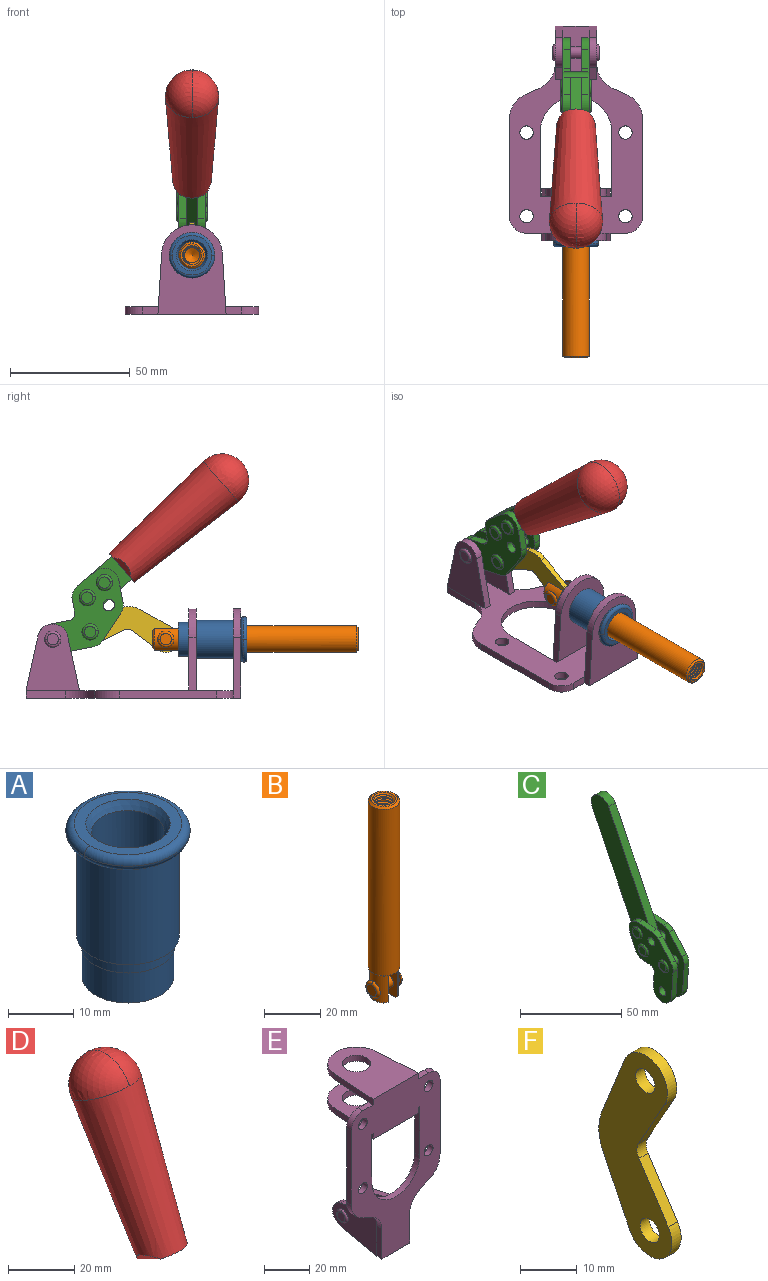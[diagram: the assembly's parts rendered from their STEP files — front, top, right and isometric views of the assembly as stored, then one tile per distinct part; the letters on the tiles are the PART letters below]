
ASSEMBLY  parts=6 mates=6
PART A: 15 faces, bbox 20.6x20.6x28.7 mm
  f0: torus R=8.26mm, axis (0,0,1), area 56.8mm2, adj f1,f10,f12
  f1: torus R=8.26mm, axis (0,0,1), area 56.8mm2, adj f0,f6,f13
  f2: cylinder r=5.59mm len=25.91mm, axis (0,0,1), area 909.6mm2, adj f3,f4
  f3: cone r=6.86mm half-angle=45deg, axis (0,0,-1), area 70.2mm2, adj f2,f14
  f4: cone r=6.47mm half-angle=30deg, axis (0,0,1), area 66.7mm2, adj f2,f13
  f5: cylinder r=7.04mm len=14.07mm, axis (0,0,1), area 252.6mm2, adj f11,f14
  f6: torus R=8.26mm, axis (0,0,1), area 56.8mm2, adj f1,f12,f13
  f7: cylinder r=7.16mm len=14.33mm, axis (0,0,1), area 91.5mm2, adj f9,f11
  f8: cylinder r=7.86mm len=18.42mm, axis (0,0,1), area 909.6mm2, adj f9,f10
  f9: plane 15.72x15.72mm, normal (0,0,-1), area 33mm2, adj f7,f8
  f10: plane 16.51x16.51mm, normal (0,0,-1), area 19.9mm2, adj f0,f8,f12
  f11: plane 14.33x14.33mm, normal (0,0,-1), area 5.7mm2, adj f5,f7
  f12: torus R=8.26mm, axis (0,0,1), area 56.8mm2, adj f0,f6,f10
  f13: plane 16.51x16.51mm, normal (0,0,1), area 82.7mm2, adj f1,f4,f6
  f14: plane 14.07x14.07mm, normal (0,0,-1), area 7.8mm2, adj f3,f5
PART B: 48 faces, bbox 12.6x11.1x86.1 mm
  f0: torus R=2.41mm, axis (-1,0,0), area 15mm2, adj f30,f32,f34
  f1: torus R=2.41mm, axis (-1,0,0), area 15mm2, adj f29,f31,f33
  f2: cylinder r=5.54mm len=72.39mm, axis (0,0,1), area 2518.5mm2, adj f3,f4,f42,f43
  f3: cone r=5.54mm half-angle=45deg, axis (0,0,1), area 7.6mm2, adj f2,f5,f41
  f4: cone r=5.54mm half-angle=45deg, axis (0,0,-1), area 34.9mm2, adj f2,f39
  f5: cylinder r=5.08mm len=11.48mm, axis (0,0,1), area 108.3mm2, adj f3,f7,f8,f41
  f6: cylinder r=2.41mm len=4.83mm, axis (-1,0,0), area 71.2mm2, adj f40,f41
  f7: cylinder r=2.41mm len=4.83mm, axis (-1,0,0), area 7.6mm2, adj f5,f34
  f8: cone r=5.08mm half-angle=45deg, axis (0,0,1), area 10.6mm2, adj f5,f37,f41
  f9: cone r=3.98mm half-angle=45deg, axis (0,0,1), area 17.6mm2, adj f27,f39,f45,f46,f47
  f10: cylinder r=2.41mm len=4.83mm, axis (-1,0,0), area 7.6mm2, adj f33,f38
  f11: cylinder r=3.2mm len=6.4mm, axis (0,0,1), area 78.4mm2, adj f12,f28,f44,f45,f47
  f12: cylinder r=3.2mm len=6.4mm, axis (0,0,1), area 10.5mm2, adj f11,f13,f45,f47
  f13: cylinder r=3.2mm len=6.4mm, axis (0,0,1), area 10.5mm2, adj f12,f14,f45,f47
  f14: cylinder r=3.2mm len=6.4mm, axis (0,0,1), area 10.5mm2, adj f13,f15,f45,f47
  f15: cylinder r=3.2mm len=6.4mm, axis (0,0,1), area 10.5mm2, adj f14,f16,f45,f47
  f16: cylinder r=3.2mm len=6.4mm, axis (0,0,1), area 10.5mm2, adj f15,f17,f45,f47
  f17: cylinder r=3.2mm len=6.4mm, axis (0,0,1), area 10.5mm2, adj f16,f18,f45,f47
  f18: cylinder r=3.2mm len=6.4mm, axis (0,0,1), area 10.5mm2, adj f17,f19,f45,f47
  f19: cylinder r=3.2mm len=6.4mm, axis (0,0,1), area 10.5mm2, adj f18,f20,f45,f47
  f20: cylinder r=3.2mm len=6.4mm, axis (0,0,1), area 10.5mm2, adj f19,f21,f45,f47
  f21: cylinder r=3.2mm len=6.4mm, axis (0,0,1), area 10.5mm2, adj f20,f22,f45,f47
  f22: cylinder r=3.2mm len=6.4mm, axis (0,0,1), area 10.5mm2, adj f21,f23,f45,f47
  f23: cylinder r=3.2mm len=6.4mm, axis (0,0,1), area 10.5mm2, adj f22,f24,f45,f47
  f24: cylinder r=3.2mm len=6.4mm, axis (0,0,1), area 10.5mm2, adj f23,f25,f45,f47
  f25: cylinder r=3.2mm len=6.4mm, axis (0,0,1), area 10.5mm2, adj f24,f26,f45,f47
  f26: cylinder r=3.2mm len=6.4mm, axis (0,0,1), area 10.5mm2, adj f25,f27,f45,f47
  f27: cylinder r=3.2mm len=6.4mm, axis (0,0,1), area 7.4mm2, adj f9,f26,f45,f47
  f28: cone r=3.2mm half-angle=60deg, axis (0,0,1), area 37.2mm2, adj f11
  f29: plane 4.83x4.83mm, normal (-1,0,0), area 18.3mm2, adj f1,f31
  f30: plane 4.83x4.83mm, normal (1,0,0), area 18.3mm2, adj f0,f32
  f31: torus R=2.41mm, axis (-1,0,0), area 15mm2, adj f1,f29,f33
  f32: torus R=2.41mm, axis (-1,0,0), area 15mm2, adj f0,f30,f34
  f33: plane 6.83x6.83mm, normal (1,0,0), area 18.3mm2, adj f1,f10,f31
  f34: plane 6.83x6.83mm, normal (-1,0,0), area 18.3mm2, adj f0,f7,f32
  f35: cone r=5.08mm half-angle=45deg, axis (0,0,1), area 10.6mm2, adj f36,f38,f40
  f36: plane 7.25x1.97mm, normal (0,0,-1), area 10mm2, adj f35,f40
  f37: plane 7.25x1.97mm, normal (0,0,-1), area 10mm2, adj f8,f41
  f38: cylinder r=5.08mm len=11.48mm, axis (0,0,1), area 108.3mm2, adj f10,f35,f40,f42
  f39: plane 9.55x9.55mm, normal (0,0,1), area 22mm2, adj f4,f9
  f40: plane 12.76x10.09mm, normal (1,0,0), area 95.7mm2, adj f6,f35,f36,f38,f42,f43
  f41: plane 12.76x10.09mm, normal (-1,0,0), area 95.7mm2, adj f3,f5,f6,f8,f37,f43
  f42: cone r=5.54mm half-angle=45deg, axis (0,0,1), area 7.6mm2, adj f2,f38,f40
  f43: plane 11.07x4.7mm, normal (0,0,-1), area 50.4mm2, adj f2,f40,f41
  f44: plane 0.89x0.62mm, normal (-1,0,0), area 0.3mm2, adj f11,f45,f46,f47
  f45: bspline ~24.8x7.63mm, area 266.6mm2, adj f9,f11,f12,f13,f14,f15,f16,f17
  f46: bspline ~24.87x7.63mm, area 73.6mm2, adj f9,f44,f45,f47
  f47: bspline ~24.98x7.63mm, area 272.5mm2, adj f9,f11,f12,f13,f14,f15,f16,f17
PART C: 59 faces, bbox 12.9x60.2x99.6 mm
  f0: torus R=2.39mm, axis (-1,0,0), area 14.9mm2, adj f20,f43,f51
  f1: torus R=2.39mm, axis (-1,0,0), area 14.9mm2, adj f19,f42,f51
  f2: torus R=2.39mm, axis (-1,0,0), area 14.9mm2, adj f18,f35,f51
  f3: torus R=2.39mm, axis (-1,0,0), area 14.9mm2, adj f14,f17,f23
  f4: torus R=2.39mm, axis (-1,0,0), area 14.9mm2, adj f13,f16,f23
  f5: torus R=2.39mm, axis (-1,0,0), area 14.9mm2, adj f12,f15,f23
  f6: cylinder r=2.39mm len=4.78mm, axis (1,0,0), area 46.5mm2, adj f48,f50,f51
  f7: cylinder r=2.39mm len=4.78mm, axis (1,0,0), area 46.5mm2, adj f50,f51
  f8: cylinder r=6.35mm len=12.68mm, axis (1,0,0), area 61.8mm2, adj f38,f39,f50,f51
  f9: cylinder r=2.39mm len=4.78mm, axis (-1,0,0), area 70.5mm2, adj f46,f50
  f10: cylinder r=2.39mm len=4.78mm, axis (-1,0,0), area 46.5mm2, adj f23,f45,f46
  f11: cylinder r=2.39mm len=4.78mm, axis (-1,0,0), area 46.5mm2, adj f23,f46
  f12: plane 4.78x4.78mm, normal (1,0,0), area 17.9mm2, adj f5,f15
  f13: plane 4.78x4.78mm, normal (1,0,0), area 17.9mm2, adj f4,f16
  f14: plane 4.78x4.78mm, normal (1,0,0), area 17.9mm2, adj f3,f17
  f15: torus R=2.39mm, axis (-1,0,0), area 14.9mm2, adj f5,f12,f23
  f16: torus R=2.39mm, axis (-1,0,0), area 14.9mm2, adj f4,f13,f23
  f17: torus R=2.39mm, axis (-1,0,0), area 14.9mm2, adj f3,f14,f23
  f18: plane 4.78x4.78mm, normal (-1,0,0), area 17.9mm2, adj f2,f35
  f19: plane 4.78x4.78mm, normal (-1,0,0), area 17.9mm2, adj f1,f42
  f20: plane 4.78x4.78mm, normal (-1,0,0), area 17.9mm2, adj f0,f43
  f21: plane 2.26x0.2mm, normal (1,0,0), area 0.2mm2, adj f31,f44
  f22: plane 2.26x0.2mm, normal (-1,0,0), area 0.2mm2, adj f41,f44
  f23: plane 39.37x30.77mm, normal (1,0,0), area 565.5mm2, adj f3,f4,f5,f10,f11,f15,f16,f17
  f24: cylinder r=6.1mm len=4.15mm, axis (-1,0,0), area 14.7mm2, adj f23,f25,f32,f46
  f25: plane 10.25x9.01mm, normal (0,-0.75,0.66), area 42.3mm2, adj f23,f24,f26,f46
  f26: cylinder r=6.35mm len=4.64mm, axis (-1,0,0), area 15.6mm2, adj f23,f25,f27,f46
  f27: plane 15.84x3.1mm, normal (0,-1,-0.07), area 49.2mm2, adj f23,f26,f28,f46
  f28: cylinder r=6.35mm len=12.68mm, axis (-1,0,0), area 61.8mm2, adj f23,f27,f29,f46
  f29: plane 8.11x3.1mm, normal (0,1,0.07), area 25.2mm2, adj f23,f28,f30,f46
  f30: cylinder r=3.05mm len=3.25mm, axis (-1,0,0), area 14.8mm2, adj f23,f29,f31,f46
  f31: plane 5.99x3.1mm, normal (0,0.07,-1), area 18.6mm2, adj f21,f23,f30,f44,f46
  f32: plane 9.5x3.1mm, normal (0,-0.07,1), area 29.5mm2, adj f23,f24,f33,f46,f47
  f33: cylinder r=6.1mm len=8.63mm, axis (-1,0,0), area 39.1mm2, adj f23,f32,f34,f47
  f34: plane 8.65x3.96mm, normal (0,0.91,-0.42), area 29.5mm2, adj f23,f33,f44,f47
  f35: torus R=2.39mm, axis (-1,0,0), area 14.9mm2, adj f2,f18,f51
  f36: plane 10.25x9.01mm, normal (0,-0.75,0.66), area 42.3mm2, adj f37,f49,f50,f51
  f37: cylinder r=6.35mm len=4.64mm, axis (1,0,0), area 15.6mm2, adj f36,f38,f50,f51
  f38: plane 15.84x3.1mm, normal (0,-1,-0.07), area 49.2mm2, adj f8,f37,f50,f51
  f39: plane 8.11x3.1mm, normal (0,1,0.07), area 25.2mm2, adj f8,f40,f50,f51
  f40: cylinder r=3.05mm len=3.25mm, axis (1,0,0), area 14.8mm2, adj f39,f41,f50,f51
  f41: plane 5.99x3.1mm, normal (0,0.07,-1), area 18.6mm2, adj f22,f40,f44,f50,f51
  f42: torus R=2.39mm, axis (-1,0,0), area 14.9mm2, adj f1,f19,f51
  f43: torus R=2.39mm, axis (-1,0,0), area 14.9mm2, adj f0,f20,f51
  f44: cylinder r=6.35mm len=12.12mm, axis (-1,0,0), area 128.9mm2, adj f21,f22,f23,f31,f34,f41,f46,f47
  f45: plane 2.65x1.35mm, normal (1,0,0), area 1mm2, adj f10,f55
  f46: plane 39.08x20.42mm, normal (-1,0,0), area 412.5mm2, adj f9,f10,f11,f24,f25,f26,f27,f28
  f47: plane 77.62x39.82mm, normal (1,0,0), area 850mm2, adj f32,f33,f34,f44,f53,f54,f55
  f48: plane 2.65x1.35mm, normal (-1,0,0), area 1mm2, adj f6,f55
  f49: cylinder r=6.1mm len=4.15mm, axis (1,0,0), area 14.7mm2, adj f36,f50,f51,f56
  f50: plane 39.08x20.42mm, normal (1,0,0), area 412.5mm2, adj f6,f7,f8,f9,f36,f37,f38,f39
  f51: plane 39.37x30.77mm, normal (-1,0,0), area 565.5mm2, adj f0,f1,f2,f6,f7,f8,f35,f36
  f52: plane 8.65x3.96mm, normal (0,0.91,-0.42), area 29.5mm2, adj f44,f51,f57,f58
  f53: plane 68.49x33.4mm, normal (0,0.9,-0.44), area 358.1mm2, adj f44,f47,f54,f58
  f54: cylinder r=6.35mm len=12.06mm, axis (1,0,0), area 93.7mm2, adj f47,f53,f55,f58
  f55: plane 68.49x33.4mm, normal (0,-0.9,0.44), area 358.1mm2, adj f44,f45,f46,f47,f48,f50,f54,f58
  f56: plane 9.5x3.1mm, normal (0,-0.07,1), area 29.5mm2, adj f49,f50,f51,f57,f58
  f57: cylinder r=6.1mm len=8.63mm, axis (1,0,0), area 39.1mm2, adj f51,f52,f56,f58
  f58: plane 77.62x39.82mm, normal (-1,0,0), area 850mm2, adj f44,f52,f53,f54,f55,f56,f57
PART D: 11 faces, bbox 22.3x42.6x64.5 mm
  f0: sphere r=11.13mm, area 411.4mm2, adj f1,f8
  f1: cone r=11.11mm half-angle=3.3deg, axis (0,0.44,0.9), area 3251.8mm2, adj f0,f7,f8,f9,f10
  f2: cylinder r=6.16mm len=11.7mm, axis (1,0,0), area 89.5mm2, adj f3,f4,f5,f6
  f3: plane 60.23x36.75mm, normal (-1,0,0), area 763.6mm2, adj f2,f4,f6,f10
  f4: plane 51.37x25.05mm, normal (0,0.9,-0.44), area 264.2mm2, adj f2,f3,f5,f10
  f5: plane 60.23x36.75mm, normal (1,0,0), area 763.6mm2, adj f2,f4,f6,f10
  f6: plane 51.37x25.05mm, normal (0,-0.9,0.44), area 264.2mm2, adj f2,f3,f5,f10
  f7: plane 9.95x5.95mm, normal (0.71,-0.31,-0.64), area 25.8mm2, adj f1,f10
  f8: sphere r=11.13mm, area 411.4mm2, adj f0,f1
  f9: plane 9.95x5.95mm, normal (-0.71,-0.31,-0.64), area 25.8mm2, adj f1,f10
  f10: plane 14.27x11.38mm, normal (0,-0.44,-0.9), area 106.7mm2, adj f1,f3,f4,f5,f6,f7,f9
PART E: 55 faces, bbox 55.7x37.4x89.8 mm
  f0: torus R=2.41mm, axis (-1,0,0), area 15mm2, adj f11,f15,f25
  f1: torus R=2.41mm, axis (-1,0,0), area 15mm2, adj f10,f12,f22
  f2: cylinder r=2.78mm len=5.56mm, axis (0,-1,0), area 54.2mm2, adj f30,f54
  f3: cylinder r=14.99mm len=29.97mm, axis (0,-1,0), area 145.9mm2, adj f30,f49,f53,f54
  f4: cylinder r=2.78mm len=5.56mm, axis (0,-1,0), area 54.2mm2, adj f30,f54
  f5: cylinder r=2.78mm len=5.56mm, axis (0,-1,0), area 54.2mm2, adj f30,f54
  f6: cylinder r=2.78mm len=5.56mm, axis (0,-1,0), area 54.2mm2, adj f30,f54
  f7: cylinder r=6.35mm len=12.7mm, axis (0,0,1), area 123.6mm2, adj f27,f51
  f8: cylinder r=6.35mm len=12.7mm, axis (0,0,-1), area 124.7mm2, adj f21,f35
  f9: cylinder r=2.41mm len=11.18mm, axis (-1,0,0), area 169.4mm2, adj f16,f19
  f10: plane 4.83x4.83mm, normal (1,0,0), area 18.3mm2, adj f1,f12
  f11: plane 4.83x4.83mm, normal (-1,0,0), area 18.3mm2, adj f0,f15
  f12: torus R=2.41mm, axis (-1,0,0), area 15mm2, adj f1,f10,f22
  f13: cylinder r=6.35mm len=12.41mm, axis (1,0,0), area 53.4mm2, adj f18,f19,f22,f23
  f14: cylinder r=6.35mm len=12.41mm, axis (-1,0,0), area 53.4mm2, adj f16,f17,f24,f25
  f15: torus R=2.41mm, axis (-1,0,0), area 15mm2, adj f0,f11,f25
  f16: plane 27.86x22.35mm, normal (1,0,0), area 425.4mm2, adj f9,f14,f17,f24,f30
  f17: plane 22.86x4.97mm, normal (0,0.21,0.98), area 72.5mm2, adj f14,f16,f25,f30
  f18: plane 22.86x4.97mm, normal (0,0.21,0.98), area 72.5mm2, adj f13,f19,f22,f30
  f19: plane 27.86x22.35mm, normal (-1,0,0), area 425.4mm2, adj f9,f13,f18,f23,f30
  f20: cylinder r=12.7mm len=25.35mm, axis (0,0,-1), area 119.8mm2, adj f21,f34,f35,f36
  f21: plane 34.21x28.07mm, normal (0,0,-1), area 702.4mm2, adj f8,f20,f30,f34,f36
  f22: plane 27.96x22.45mm, normal (1,0,0), area 407.2mm2, adj f1,f12,f13,f18,f23,f30,f42,f43
  f23: plane 22.86x4.97mm, normal (0,0.21,-0.98), area 72.5mm2, adj f13,f19,f22,f44
  f24: plane 22.86x4.97mm, normal (0,0.21,-0.98), area 72.5mm2, adj f14,f16,f25,f44
  f25: plane 27.86x22.35mm, normal (-1,0,0), area 407.1mm2, adj f0,f14,f15,f17,f24,f30,f45,f46
  f26: plane 3.1x0.95mm, normal (0,0,-1), area 2.7mm2, adj f30,f49,f50,f54
  f27: plane 34.21x28.07mm, normal (0,0,1), area 702.4mm2, adj f7,f28,f30,f50,f52
  f28: cylinder r=12.7mm len=25.35mm, axis (0,0,1), area 118.8mm2, adj f27,f50,f51,f52
  f29: plane 3.1x0.95mm, normal (0,0,-1), area 2.7mm2, adj f30,f52,f53,f54
  f30: plane 86.54x55.63mm, normal (0,1,0), area 2362.9mm2, adj f2,f3,f4,f5,f6,f16,f17,f18
  f31: plane 40.56x3.1mm, normal (-1,0,0), area 125.7mm2, adj f30,f32,f48,f54
  f32: cylinder r=7.11mm len=7.11mm, axis (0,-1,0), area 34.6mm2, adj f30,f31,f33,f54
  f33: plane 6.67x3.1mm, normal (0,0,1), area 20.4mm2, adj f30,f32,f34,f54
  f34: plane 25.39x3.13mm, normal (-1,0.06,0), area 79.5mm2, adj f20,f21,f33,f35,f54
  f35: plane 37.31x28.45mm, normal (0,0,1), area 789.9mm2, adj f8,f20,f34,f36,f54
  f36: plane 25.39x3.13mm, normal (1,0.06,0), area 79.5mm2, adj f20,f21,f35,f37,f54
  f37: plane 6.67x3.1mm, normal (0,0,1), area 20.4mm2, adj f30,f36,f38,f54
  f38: cylinder r=7.11mm len=7.11mm, axis (0,-1,0), area 34.6mm2, adj f30,f37,f39,f54
  f39: plane 40.56x3.1mm, normal (1,0,0), area 125.7mm2, adj f30,f38,f40,f54
  f40: cylinder r=11.18mm len=10.16mm, axis (0,-1,0), area 39.5mm2, adj f30,f39,f41,f54
  f41: plane 6.09x3.1mm, normal (0.42,0,-0.91), area 20.8mm2, adj f30,f40,f42,f54
  f42: cylinder r=11.18mm len=9.41mm, axis (0,-1,0), area 37.2mm2, adj f22,f30,f41,f43,f54
  f43: plane 16.5x3.1mm, normal (1,0,0), area 51.1mm2, adj f22,f42,f44,f54
  f44: plane 17.37x3.1mm, normal (0,0,-1), area 53.8mm2, adj f23,f24,f30,f43,f45,f54
  f45: plane 16.5x3.1mm, normal (-1,0,0), area 51.1mm2, adj f25,f44,f46,f54
  f46: cylinder r=11.18mm len=9.41mm, axis (0,-1,0), area 37.2mm2, adj f25,f30,f45,f47,f54
  f47: plane 6.09x3.1mm, normal (-0.42,0,-0.91), area 20.8mm2, adj f30,f46,f48,f54
  f48: cylinder r=11.18mm len=10.16mm, axis (0,-1,0), area 39.5mm2, adj f30,f31,f47,f54
  f49: plane 26.54x3.1mm, normal (-1,0,0), area 82.3mm2, adj f3,f26,f30,f54
  f50: plane 25.39x3.1mm, normal (1,0.06,0), area 78.8mm2, adj f26,f27,f28,f51,f54
  f51: plane 37.31x28.45mm, normal (0,0,-1), area 789.9mm2, adj f7,f28,f50,f52,f54
  f52: plane 25.39x3.1mm, normal (-1,0.06,0), area 78.8mm2, adj f27,f28,f29,f51,f54
  f53: plane 26.54x3.1mm, normal (1,0,0), area 82.3mm2, adj f3,f29,f30,f54
  f54: plane 89.66x55.63mm, normal (0,-1,0), area 2678.5mm2, adj f2,f3,f4,f5,f6,f26,f29,f31
PART F: 12 faces, bbox 2.3x18.2x42.8 mm
  f0: cylinder r=2.4mm len=4.8mm, axis (1,0,0), area 34.9mm2, adj f4,f11
  f1: cylinder r=10.41mm len=8.47mm, axis (1,0,0), area 20.2mm2, adj f4,f9,f10,f11
  f2: cylinder r=3.05mm len=3.16mm, axis (1,0,0), area 7.7mm2, adj f4,f6,f7,f11
  f3: cylinder r=2.4mm len=4.8mm, axis (1,0,0), area 34.9mm2, adj f4,f11
  f4: plane 42.81x18.23mm, normal (-1,0,0), area 414.1mm2, adj f0,f1,f2,f3,f5,f6,f7,f8
  f5: cylinder r=5.54mm len=10.67mm, axis (1,0,0), area 41.8mm2, adj f4,f6,f10,f11
  f6: plane 11.66x6.53mm, normal (0,-0.87,-0.49), area 30.9mm2, adj f2,f4,f5,f11
  f7: plane 11.17x7.33mm, normal (0,-0.84,0.55), area 30.9mm2, adj f2,f4,f8,f11
  f8: cylinder r=5.54mm len=10.51mm, axis (1,0,0), area 41.8mm2, adj f4,f7,f9,f11
  f9: plane 13.67x6.67mm, normal (0,0.9,-0.44), area 35.1mm2, adj f1,f4,f8,f11
  f10: plane 14.1x5.7mm, normal (0,0.93,0.37), area 35.1mm2, adj f1,f4,f5,f11
  f11: plane 42.81x18.23mm, normal (1,0,0), area 414.1mm2, adj f0,f1,f2,f3,f5,f6,f7,f8
PLACE A rot(axis=(1,0,0),90deg) t=(0,9.14,0)mm
PLACE B rot(axis=(1,0,0),90deg) t=(0,9.52,0)mm
PLACE C rot(axis=(1,0,0),75deg) t=(0,3.86,9.14)mm
PLACE D rot(axis=(1,0,0),75deg) t=(0,3.86,9.14)mm
PLACE E rot(axis=(1,0,0),90deg) t=(0,9.14,0)mm fixed
PLACE F rot(axis=(1,0,0),97.5deg) t=(0,12.59,2.22)mm
MATE fastened A.f2 <-> E.f7  axis (0,1,0) through (0,-37.25,24.61)mm
MATE revolute F.f5 <-> B.f6  axis (1,0,0) through (0,-5.96,24.61)mm
MATE fastened C.f54 <-> D.f2  axis (1,0,0) through (0,-30.66,91.94)mm
MATE revolute F.f3 <-> C.f4  axis (1,0,0) through (0,25.65,27.64)mm
MATE revolute C.f7 <-> E.f0  axis (1,0,0) through (0,41.23,24.61)mm
MATE slider B.f2 <-> A.f2  axis (0,-1,0) through (0,-49.26,24.61)mm
